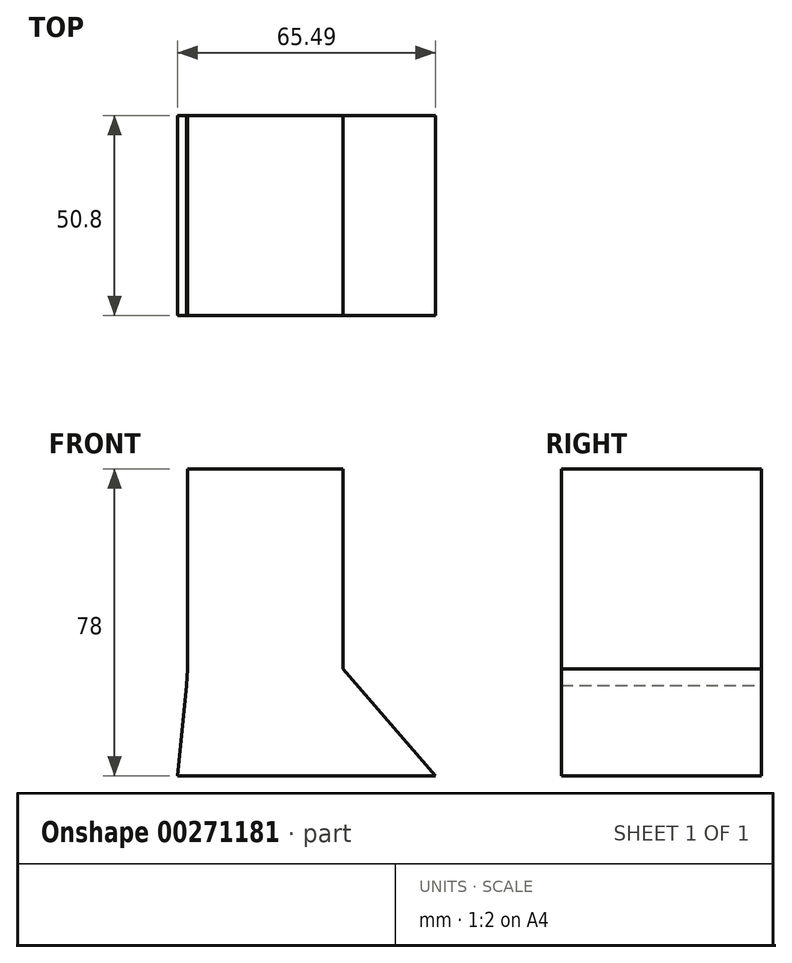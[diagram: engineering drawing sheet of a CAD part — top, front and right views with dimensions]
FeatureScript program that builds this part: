
annotation { "Feature Type Name" : "Feature", "Feature Type Description" : "" }
export const myFeature = defineFeature(function(context is Context, id is Id, definition is map)
    precondition{}
    {
        {
            var Q0;
            Q0=qCreatedBy(makeId("Front.planeOp"),FACE);
            var sketch = newSketch(context, id + "F0", { "sketchPlane" : qUnion([Q0])});
            skLineSegment(sketch, "E0", {"start": v(36.47, 0) * mm, "end": v(19.89, 19.24) * mm});
            skLineSegment(sketch, "E1", {"start": v(19.89, 19.24) * mm, "end": v(19.89, 70.04) * mm});
            skLineSegment(sketch, "E2", {"start": v(36.47, 0) * mm, "end": v(43.34, -7.96) * mm});
            skLineSegment(sketch, "E3", {"start": v(19.89, 70.04) * mm, "end": v(-19.62, 70.04) * mm});
            skLineSegment(sketch, "E4", {"start": v(-19.62, 70.04) * mm, "end": v(-19.62, 19.24) * mm});
            skLineSegment(sketch, "E5", {"start": v(43.34, -7.96) * mm, "end": v(-22.15, -7.96) * mm});
            skLineSegment(sketch, "E6", {"start": v(-22.15, -7.96) * mm, "end": v(-19.62, 17.3) * mm});
            skLineSegment(sketch, "E7", {"start": v(-19.62, 19.24) * mm, "end": v(-19.84, 15.08) * mm});
            skSolve(sketch);
        }
        {
            var Q0;
            Q0 = qSketchRegion(id + "F0", true);
            extrude(context, id + "F1", {"entities" : qUnion([Q0]), "depth" : 50.8 * mm});
        }
    });
